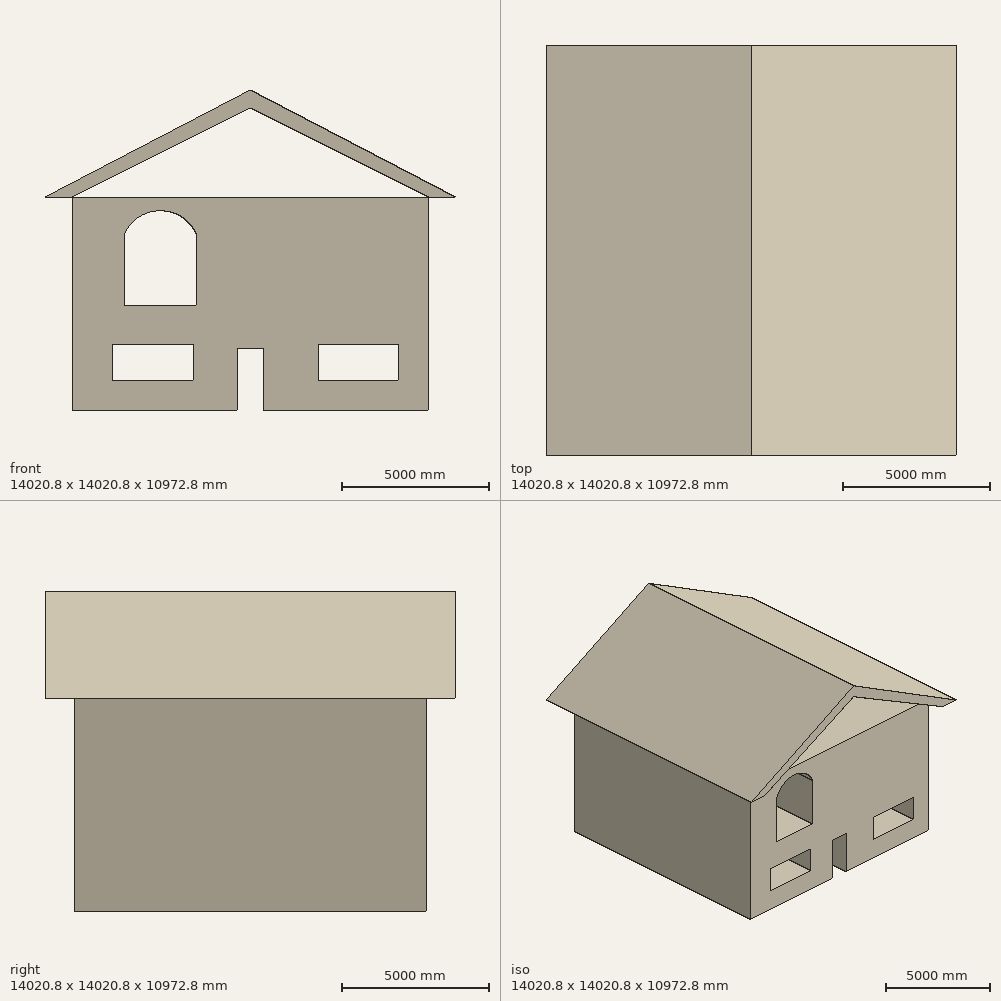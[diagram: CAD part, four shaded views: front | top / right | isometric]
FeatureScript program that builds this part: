
annotation { "Feature Type Name" : "Feature", "Feature Type Description" : "" }
export const myFeature = defineFeature(function(context is Context, id is Id, definition is map)
    precondition{}
    {
        {
            var Q0;
            Q0=qCreatedBy(makeId("Front.planeOp"),FACE);
            var sketch = newSketch(context, id + "F0", { "sketchPlane" : qUnion([Q0])});
            skLineSegment(sketch, "E0", {"start": v(0, 0) * mm, "end": v(6096, 0) * mm});
            skLineSegment(sketch, "E1", {"start": v(0, 0) * mm, "end": v(-6096, 0) * mm});
            skLineSegment(sketch, "E2", {"start": v(0, 0) * mm, "end": v(0, 3048) * mm, "construction": true});
            skLineSegment(sketch, "E3", {"start": v(-6096, 0) * mm, "end": v(0, 3048) * mm});
            skLineSegment(sketch, "E4", {"start": v(0, 3048) * mm, "end": v(6096, 0) * mm});
            skLineSegment(sketch, "E5", {"start": v(-6096, 0) * mm, "end": v(-7010.4, 0) * mm});
            skLineSegment(sketch, "E6", {"start": v(6096, 0) * mm, "end": v(7010.4, 0) * mm});
            skLineSegment(sketch, "E7", {"start": v(0, 3048) * mm, "end": v(0, 3657.6) * mm});
            skLineSegment(sketch, "E8", {"start": v(0, 3657.6) * mm, "end": v(7010.4, 0) * mm});
            skLineSegment(sketch, "E9", {"start": v(0, 3657.6) * mm, "end": v(-7010.4, 0) * mm});
            skLineSegment(sketch, "E10", {"start": v(-6096, 0) * mm, "end": v(-6096, -7315.2) * mm});
            skLineSegment(sketch, "E11", {"start": v(6096, 0) * mm, "end": v(6096, -7315.2) * mm});
            skLineSegment(sketch, "E12", {"start": v(-6096, -7315.2) * mm, "end": v(6096, -7315.2) * mm});
            skLineSegment(sketch, "E13", {"start": v(-6096, -7315.2) * mm, "end": v(-6096, -7620) * mm});
            skLineSegment(sketch, "E14", {"start": v(6096, -7315.2) * mm, "end": v(6096, -7620) * mm});
            skLineSegment(sketch, "E15", {"start": v(-457.2, -7315.2) * mm, "end": v(0, -7315.2) * mm});
            skLineSegment(sketch, "E16", {"start": v(0, -7315.2) * mm, "end": v(457.2, -7315.2) * mm});
            skLineSegment(sketch, "E17", {"start": v(-457.2, -7315.2) * mm, "end": v(-457.2, -5181.6) * mm});
            skLineSegment(sketch, "E18", {"start": v(457.2, -7315.2) * mm, "end": v(457.2, -5181.6) * mm});
            skLineSegment(sketch, "E19", {"start": v(-457.2, -5181.6) * mm, "end": v(457.2, -5181.6) * mm});
            skLineSegment(sketch, "E20.bottom", {"start": v(2562.93, -5181.6) * mm, "end": v(4696.53, -5181.6) * mm});
            skLineSegment(sketch, "E20.top", {"start": v(2562.93, -6096) * mm, "end": v(4696.53, -6096) * mm});
            skLineSegment(sketch, "E20.left", {"start": v(2562.93, -5181.6) * mm, "end": v(2562.93, -6096) * mm});
            skLineSegment(sketch, "E20.right", {"start": v(4696.53, -5181.6) * mm, "end": v(4696.53, -6096) * mm});
            skLineSegment(sketch, "E21.bottom", {"start": v(-4448.48, -5181.6) * mm, "end": v(-2314.88, -5181.6) * mm});
            skLineSegment(sketch, "E21.top", {"start": v(-4448.48, -6096) * mm, "end": v(-2314.88, -6096) * mm});
            skLineSegment(sketch, "E21.left", {"start": v(-4448.48, -5181.6) * mm, "end": v(-4448.48, -6096) * mm});
            skLineSegment(sketch, "E21.right", {"start": v(-2314.88, -5181.6) * mm, "end": v(-2314.88, -6096) * mm});
            skLineSegment(sketch, "E22.bottom", {"start": v(-4704.73, -5057.75) * mm, "end": v(-1961.53, -5057.75) * mm});
            skLineSegment(sketch, "E22.top", {"start": v(-4704.73, -6276.95) * mm, "end": v(-1961.53, -6276.95) * mm});
            skLineSegment(sketch, "E22.left", {"start": v(-4704.73, -5057.75) * mm, "end": v(-4704.73, -6276.95) * mm});
            skLineSegment(sketch, "E22.right", {"start": v(-1961.53, -5057.75) * mm, "end": v(-1961.53, -6276.95) * mm});
            skLineSegment(sketch, "E23.bottom", {"start": v(2314.88, -5057.75) * mm, "end": v(5058.08, -5057.75) * mm});
            skLineSegment(sketch, "E23.top", {"start": v(2314.88, -6276.95) * mm, "end": v(5058.08, -6276.95) * mm});
            skLineSegment(sketch, "E23.left", {"start": v(2314.88, -5057.75) * mm, "end": v(2314.88, -6276.95) * mm});
            skLineSegment(sketch, "E23.right", {"start": v(5058.08, -5057.75) * mm, "end": v(5058.08, -6276.95) * mm});
            skLineSegment(sketch, "E24.bottom", {"start": v(-4295.88, -1256.7) * mm, "end": v(-1857.48, -1256.7) * mm});
            skLineSegment(sketch, "E24.top", {"start": v(-4295.88, -3695.1) * mm, "end": v(-1857.48, -3695.1) * mm});
            skLineSegment(sketch, "E24.left", {"start": v(-4295.88, -1256.7) * mm, "end": v(-4295.88, -3695.1) * mm});
            skLineSegment(sketch, "E24.right", {"start": v(-1857.48, -1256.7) * mm, "end": v(-1857.48, -3695.1) * mm});
            skArc(sketch, "E25", {"start": v(-1857.48, -1256.7) * mm, "mid": v(-3076.68, -469.15) * mm, "end": v(-4295.88, -1256.7) * mm});
            skSolve(sketch);
        }
        {
            var Q0;
            Q0=makeQuery(id+"F0.imprint","IMPRINT",FACE,{"disambiguationData":[TD([[makeQuery(id+"F0.imprint","IMPRINT",EDGE,{"derivedFrom":sQuery(id+"F0.wireOp",EDGE,"E4")}),1.0]])]});
            var Q1;
            Q1=makeQuery(id+"F0.imprint","IMPRINT",FACE,{"disambiguationData":[TD([[makeQuery(id+"F0.imprint","IMPRINT",EDGE,{"derivedFrom":sQuery(id+"F0.wireOp",EDGE,"E3")}),1.0]])]});
            extrude(context, id + "F1", {"entities" : qUnion([Q0, Q1]), "endBound" : BoundingType.SYMMETRIC, "depth" : 14020.8 * mm, "offsetDistance" : 30.48 * mm});
        }
        {
            var Q0;
            Q0=makeQuery(id+"F0.imprint","IMPRINT",FACE,{"disambiguationData":[TD([[makeQuery(id+"F0.imprint","IMPRINT",EDGE,{"derivedFrom":sQuery(id+"F0.wireOp",EDGE,"E0")}),-1.0]])]});
            extrude(context, id + "F2", {"entities" : qUnion([Q0]), "endBound" : BoundingType.SYMMETRIC, "depth" : 12039.6 * mm, "offsetDistance" : 30.48 * mm});
        }
    });
